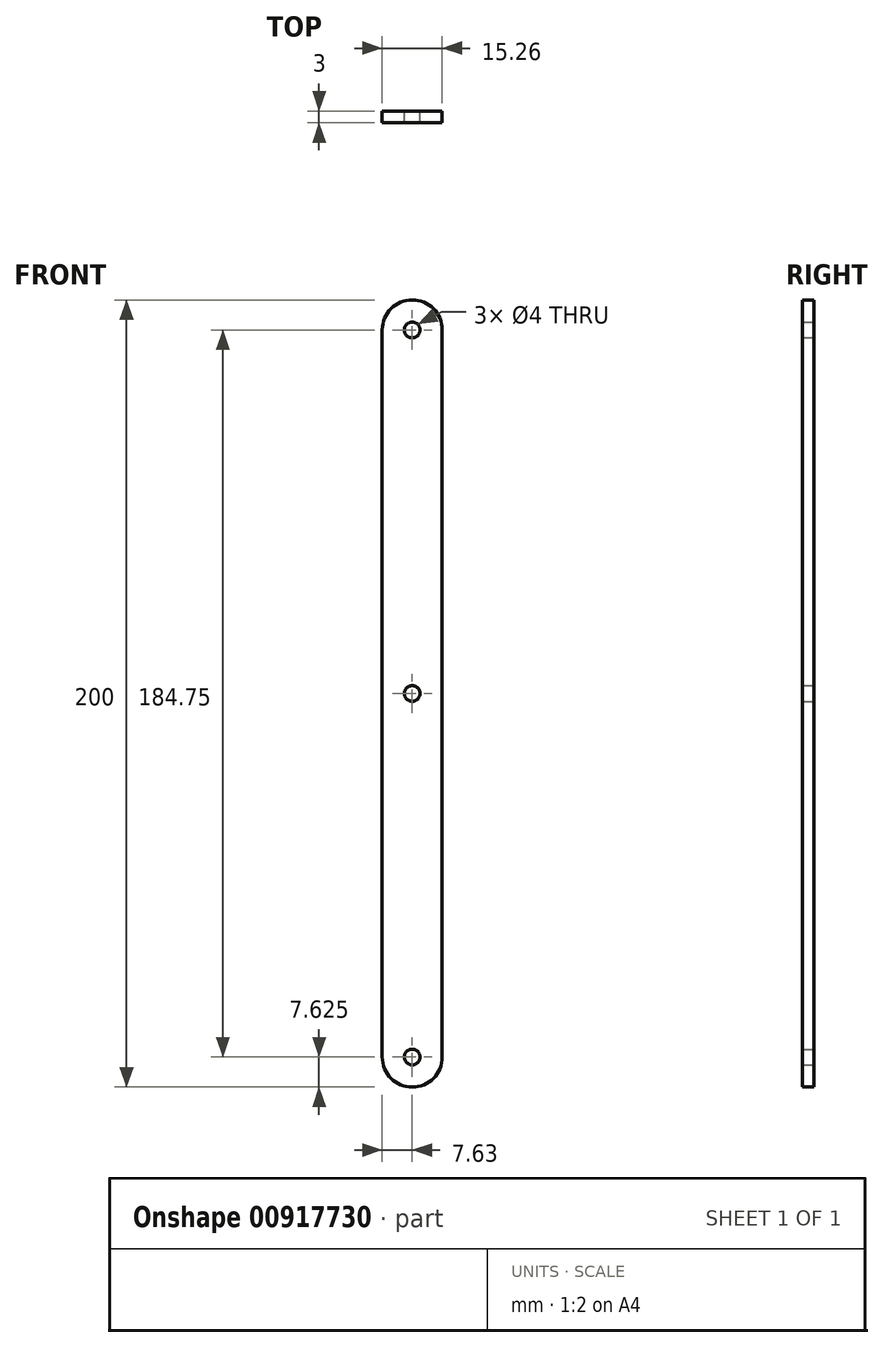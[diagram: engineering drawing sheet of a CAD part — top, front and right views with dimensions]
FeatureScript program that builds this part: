
annotation { "Feature Type Name" : "Feature", "Feature Type Description" : "" }
export const myFeature = defineFeature(function(context is Context, id is Id, definition is map)
    precondition{}
    {
        {
            var Q0;
            Q0=qCreatedBy(makeId("Front.planeOp"),FACE);
            var sketch = newSketch(context, id + "F0", { "sketchPlane" : qUnion([Q0])});
            skLineSegment(sketch, "E0", {"start": v(-7.62, 92.38) * mm, "end": v(-7.62, -92.38) * mm});
            skLineSegment(sketch, "E1", {"start": v(7.63, 92.38) * mm, "end": v(7.63, -92.38) * mm});
            skArc(sketch, "E2", {"start": v(7.63, 92.38) * mm, "mid": v(0, 100) * mm, "end": v(-7.62, 92.38) * mm});
            skArc(sketch, "E3", {"start": v(-7.62, -92.37) * mm, "mid": v(0, -100) * mm, "end": v(7.63, -92.38) * mm});
            skCircle(sketch, "E4", {"center": v(0, 92.38) * mm, "radius": 2 * mm});
            skCircle(sketch, "E5", {"center": v(0, -92.38) * mm, "radius": 2 * mm});
            skLineSegment(sketch, "E6", {"start": v(-7.62, 0) * mm, "end": v(7.63, 0) * mm});
            skLineSegment(sketch, "E7", {"start": v(0, 100) * mm, "end": v(0, 0) * mm});
            skCircle(sketch, "E8", {"center": v(0, 0) * mm, "radius": 2 * mm});
            skLineSegment(sketch, "E9", {"start": v(0, -100) * mm, "end": v(0, 0) * mm});
            skSolve(sketch);
        }
        {
            var Q0;
            {var subQ0=sQuery(id+"F0.wireOp",EDGE,"E2");Q0=makeQuery(id+"F0.imprint","IMPRINT",FACE,{"disambiguationData":[TD([[makeQuery(id+"F0.imprint","IMPRINT",EDGE,{"derivedFrom":subQ0}),1.0]])]});}
            var Q1;
            {var subQ0=sQuery(id+"F0.wireOp",EDGE,"E3");Q1=makeQuery(id+"F0.imprint","IMPRINT",FACE,{"disambiguationData":[TD([[makeQuery(id+"F0.imprint","IMPRINT",EDGE,{"derivedFrom":subQ0}),1.0]])]});}
            extrude(context, id + "F1", {"entities" : qUnion([Q0, Q1]), "depth" : 3 * mm, "offsetDistance" : 25 * mm, "symmetric" : true});
        }
    });
